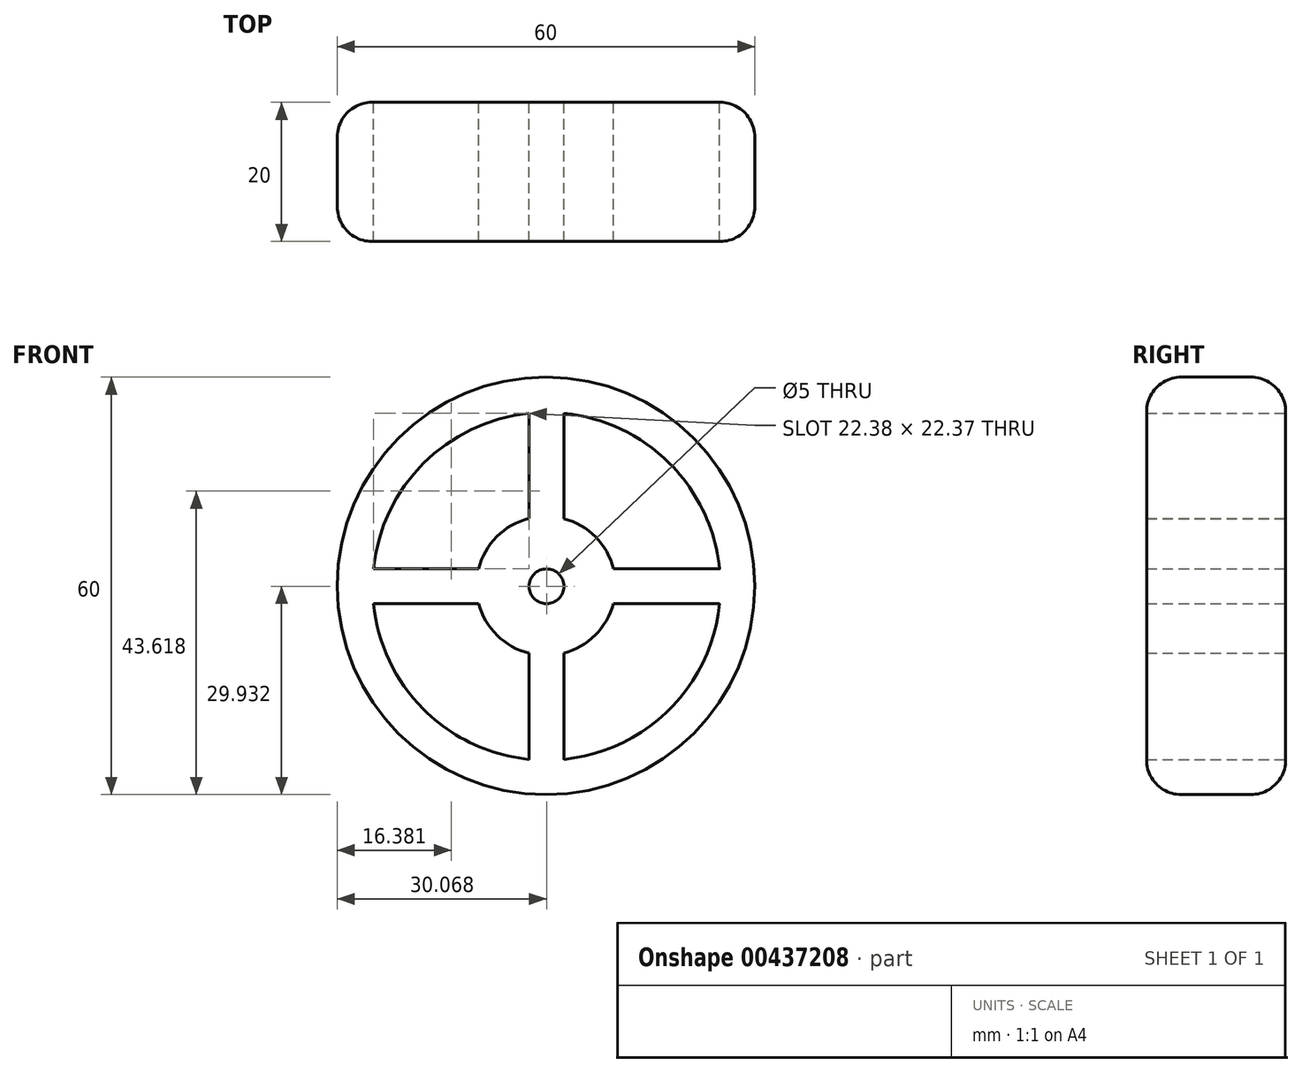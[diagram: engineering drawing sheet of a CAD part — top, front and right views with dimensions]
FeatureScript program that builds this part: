
annotation { "Feature Type Name" : "Feature", "Feature Type Description" : "" }
export const myFeature = defineFeature(function(context is Context, id is Id, definition is map)
    precondition{}
    {
        {
            var Q0;
            Q0=qCreatedBy(makeId("Front.planeOp"),FACE);
            var sketch = newSketch(context, id + "F0", { "sketchPlane" : qUnion([Q0])});
            skCircle(sketch, "E0", {"center": v(0, 0) * mm, "radius": 30 * mm});
            skArc(sketch, "E1", {"start": v(-2.43, 24.8) * mm, "mid": v(-17.6, 17.6) * mm, "end": v(-24.8, 2.43) * mm});
            skArc(sketch, "E2", {"start": v(9.7, 2.43) * mm, "mid": v(7.12, 7.02) * mm, "end": v(2.57, 9.66) * mm});
            skCircle(sketch, "E3", {"center": v(0.07, -0.07) * mm, "radius": 2.5 * mm});
            skLineSegment(sketch, "E4", {"start": v(0.07, 2.43) * mm, "end": v(0.07, 30) * mm});
            skLineSegment(sketch, "E5", {"start": v(0.07, -2.57) * mm, "end": v(0.07, -30) * mm});
            skLineSegment(sketch, "E6", {"start": v(2.57, -0.07) * mm, "end": v(30, -0.07) * mm});
            skLineSegment(sketch, "E7", {"start": v(-2.43, -0.07) * mm, "end": v(-30, -0.07) * mm});
            skLineSegment(sketch, "E8", {"start": v(0, 2.43) * mm, "end": v(0.07, 2.43) * mm});
            skArc(sketch, "E9.trimOffspring", {"start": v(-24.8, -2.57) * mm, "mid": v(-17.6, -17.75) * mm, "end": v(-2.43, -24.94) * mm});
            skArc(sketch, "E10.trimOffspring", {"start": v(24.94, 2.43) * mm, "mid": v(17.75, 17.6) * mm, "end": v(2.57, 24.8) * mm});
            skArc(sketch, "E11.trimOffspring", {"start": v(2.57, -24.94) * mm, "mid": v(17.75, -17.75) * mm, "end": v(24.94, -2.57) * mm});
            skLineSegment(sketch, "E12.trimOffspring", {"start": v(-2.43, 9.7) * mm, "end": v(-2.43, 24.8) * mm});
            skLineSegment(sketch, "E13.trimOffspring", {"start": v(2.57, 9.66) * mm, "end": v(2.57, 24.8) * mm});
            skLineSegment(sketch, "E14.trimOffspring", {"start": v(-9.7, 2.43) * mm, "end": v(-24.8, 2.43) * mm});
            skLineSegment(sketch, "E15.trimOffspring", {"start": v(-9.66, -2.57) * mm, "end": v(-24.8, -2.57) * mm});
            skLineSegment(sketch, "E16.trimOffspring", {"start": v(-2.43, -9.7) * mm, "end": v(-2.43, -24.94) * mm});
            skLineSegment(sketch, "E17.trimOffspring", {"start": v(2.57, -9.66) * mm, "end": v(2.57, -24.94) * mm});
            skLineSegment(sketch, "E18.trimOffspring", {"start": v(9.66, -2.57) * mm, "end": v(24.94, -2.57) * mm});
            skLineSegment(sketch, "E19.trimOffspring", {"start": v(9.7, 2.43) * mm, "end": v(24.94, 2.43) * mm});
            skArc(sketch, "E20.trimOffspring", {"start": v(-2.43, 9.7) * mm, "mid": v(-7.07, 7.07) * mm, "end": v(-9.7, 2.43) * mm});
            skArc(sketch, "E21.trimOffspring", {"start": v(-9.66, -2.57) * mm, "mid": v(-7.02, -7.12) * mm, "end": v(-2.43, -9.7) * mm});
            skArc(sketch, "E22.trimOffspring", {"start": v(2.57, -9.66) * mm, "mid": v(7.07, -7.07) * mm, "end": v(9.66, -2.57) * mm});
            skSolve(sketch);
        }
        {
            var Q0;
            Q0 = qSketchRegion(id + "F0", true);
            extrude(context, id + "F1", {"entities" : qUnion([Q0]), "depth" : 20 * mm});
        }
        {
            var Q0;
            Q0=makeQuery(id+"F1.opExtrude","CAP_EDGE",EDGE,{"disambiguationData":[OSD([sQuery(id+"F0.wireOp",EDGE,"E0")])],"isStart":false});
            fillet(context, id + "F2", {"entities" : qUnion([Q0]), "radius" : 5 * mm, "tangentPropagation" : true, "allowEdgeOverflow" : false});
        }
        {
            var Q0;
            Q0=makeQuery(id+"F1.opExtrude","CAP_EDGE",EDGE,{"disambiguationData":[OSD([sQuery(id+"F0.wireOp",EDGE,"E0")])],"isStart":true});
            fillet(context, id + "F3", {"entities" : qUnion([Q0]), "radius" : 5 * mm, "tangentPropagation" : true, "allowEdgeOverflow" : false});
        }
    });
